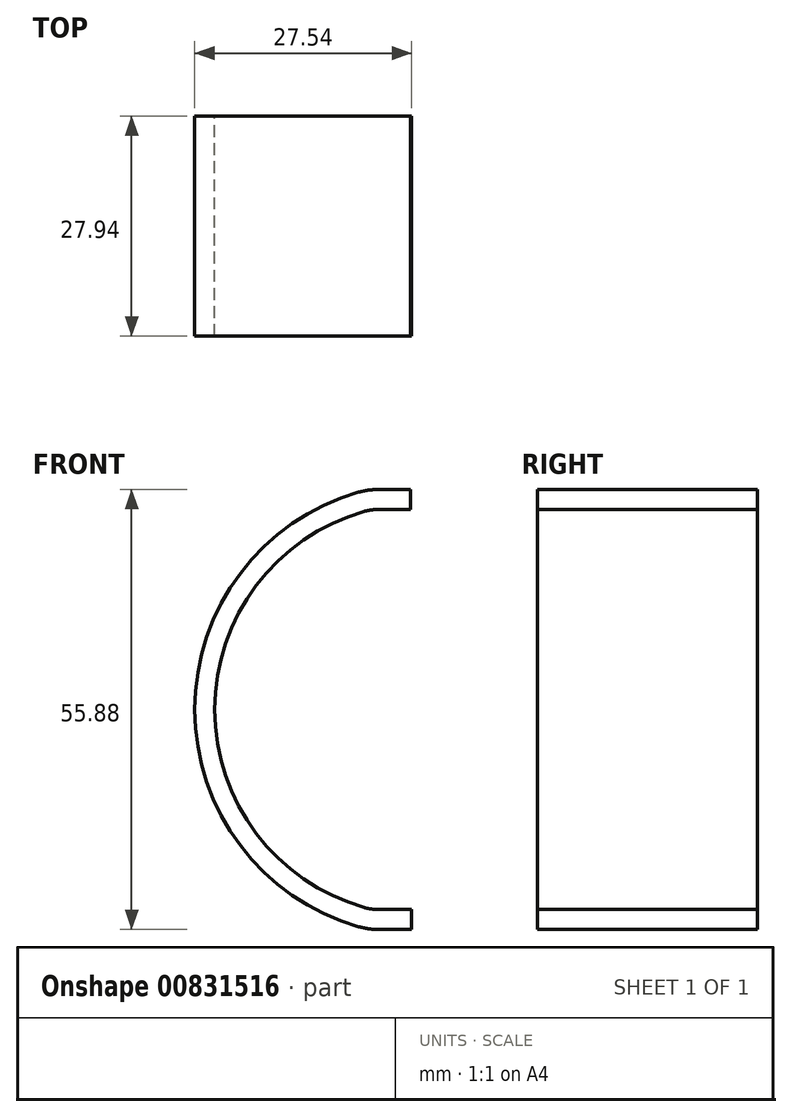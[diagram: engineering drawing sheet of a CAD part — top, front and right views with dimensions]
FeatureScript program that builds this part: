
annotation { "Feature Type Name" : "Feature", "Feature Type Description" : "" }
export const myFeature = defineFeature(function(context is Context, id is Id, definition is map)
    precondition{}
    {
        {
            var Q0;
            Q0=qCreatedBy(makeId("Right.planeOp"),FACE);
            cPlane(context, id + "F0", {"entities" : qUnion([Q0]), "cplaneType" : CPlaneType.OFFSET, "offset" : 5.08 * mm, "width" : 152.4 * mm, "height" : 152.4 * mm});
        }
        {
            var Q0;
            Q0=qCreatedBy(makeId("Front.planeOp"),FACE);
            var sketch = newSketch(context, id + "F1", { "sketchPlane" : qUnion([Q0])});
            skArc(sketch, "E0", {"start": v(-1.11, 26.38) * mm, "mid": v(-21.01, 0) * mm, "end": v(-1.11, -26.38) * mm});
            skLineSegment(sketch, "E1", {"start": v(0.98, 26.67) * mm, "end": v(5.13, 26.67) * mm});
            skLineSegment(sketch, "E2", {"start": v(0.98, -26.67) * mm, "end": v(5.26, -26.67) * mm});
            skPoint(sketch, "E3.visualSharp", {"position": v(0, 26.67) * mm});
            skArc(sketch, "E3.filletArc", {"start": v(0.98, 26.67) * mm, "mid": v(-0.08, 26.6) * mm, "end": v(-1.11, 26.38) * mm});
            skPoint(sketch, "E4.visualSharp", {"position": v(0, -26.67) * mm});
            skArc(sketch, "E4.filletArc", {"start": v(-1.11, -26.38) * mm, "mid": v(-0.08, -26.6) * mm, "end": v(0.98, -26.67) * mm});
            skSolve(sketch);
        }
        {
            var Q0;
            Q0=qCreatedBy(id+"F0.planeOp",FACE);
            var sketch = newSketch(context, id + "F2", { "sketchPlane" : qUnion([Q0])});
            skLineSegment(sketch, "E5.bottom", {"start": v(-13.97, 27.94) * mm, "end": v(13.97, 27.94) * mm});
            skLineSegment(sketch, "E5.top", {"start": v(-13.97, 25.4) * mm, "end": v(13.97, 25.4) * mm});
            skLineSegment(sketch, "E5.left", {"start": v(-13.97, 27.94) * mm, "end": v(-13.97, 25.4) * mm});
            skLineSegment(sketch, "E5.right", {"start": v(13.97, 27.94) * mm, "end": v(13.97, 25.4) * mm});
            skSolve(sketch);
        }
        {
            var Q0;
            Q0=makeQuery(id+"F2.imprint","IMPRINT",FACE,{"disambiguationData":[TD([[makeQuery(id+"F2.imprint","IMPRINT",EDGE,{"derivedFrom":sQuery(id+"F2.wireOp",EDGE,"E5.bottom")}),-1.0]])]});
            var Q1;
            Q1=sQuery(id+"F1.wireOp",EDGE,"E0");
            var Q2;
            Q2=sQuery(id+"F1.wireOp",EDGE,"E1");
            var Q3;
            Q3=sQuery(id+"F1.wireOp",EDGE,"E3.filletArc");
            var Q4;
            Q4=sQuery(id+"F1.wireOp",EDGE,"E4.filletArc");
            var Q5;
            Q5=sQuery(id+"F1.wireOp",EDGE,"E2");
            sweep(context, id + "F3", {"profiles" : qUnion([Q0]), "path" : qUnion([Q1, Q2, Q3, Q4, Q5])});
        }
    });
